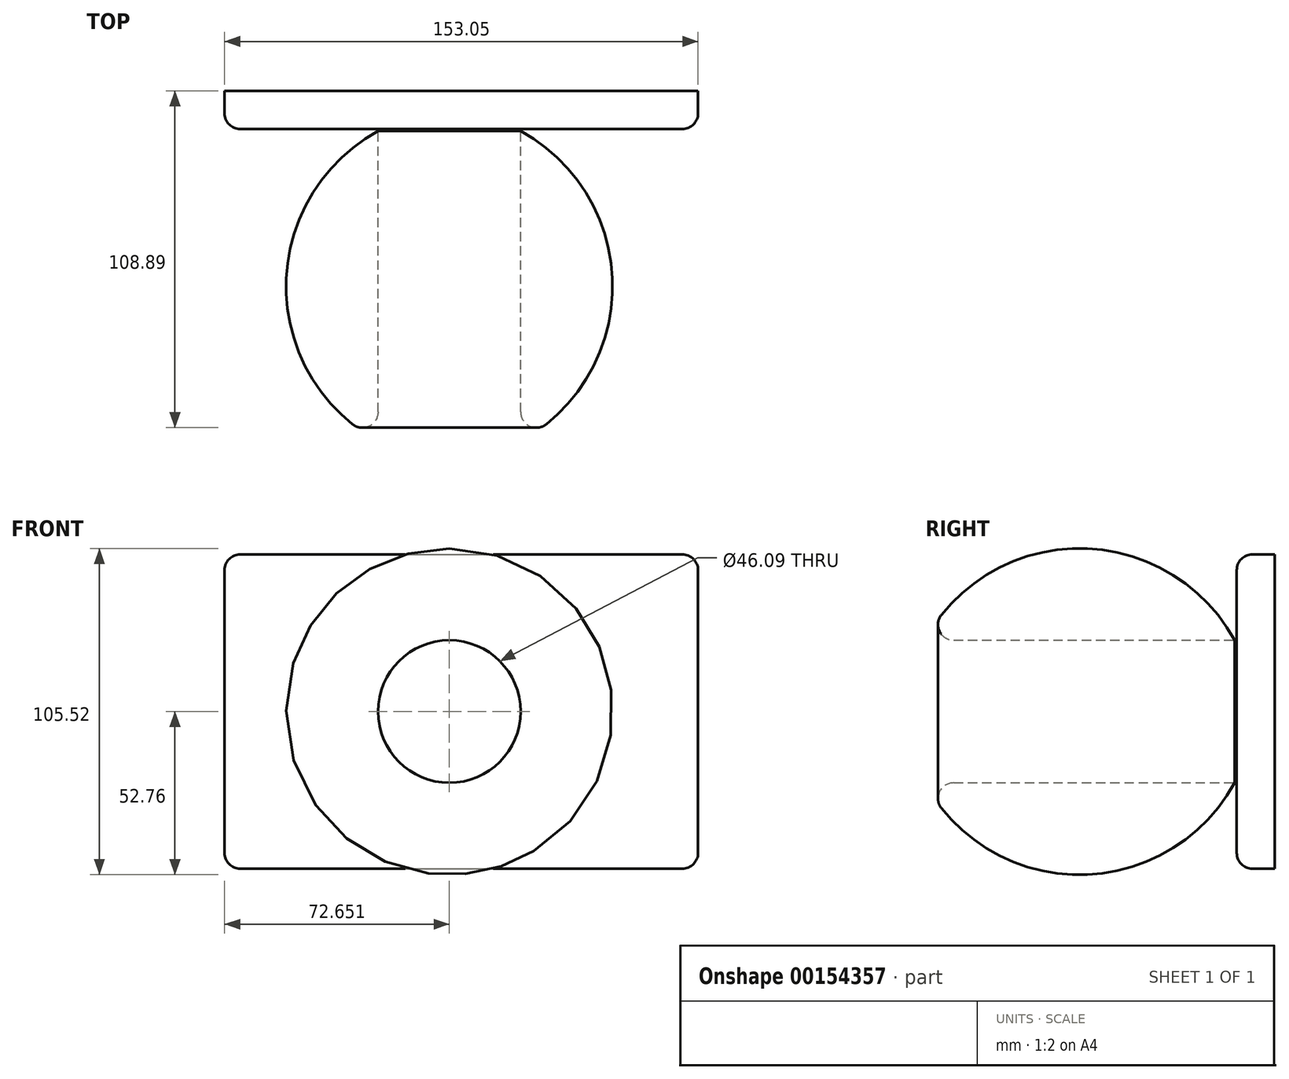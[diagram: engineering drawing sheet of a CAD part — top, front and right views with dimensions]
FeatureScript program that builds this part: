
annotation { "Feature Type Name" : "Feature", "Feature Type Description" : "" }
export const myFeature = defineFeature(function(context is Context, id is Id, definition is map)
    precondition{}
    {
        {
            var Q0;
            Q0=qCreatedBy(makeId("Top.planeOp"),FACE);
            var sketch = newSketch(context, id + "F0", { "sketchPlane" : qUnion([Q0])});
            skLineSegment(sketch, "E0", {"start": v(-59.4, 58.59) * mm, "end": v(-59.4, -41.7) * mm});
            skLineSegment(sketch, "E1", {"start": v(-36.35, 58.59) * mm, "end": v(-36.35, -41.7) * mm});
            skArc(sketch, "E2", {"start": v(-36.35, -41.7) * mm, "mid": v(-6.64, 8.44) * mm, "end": v(-36.35, 58.59) * mm});
            skSolve(sketch);
        }
        {
            var Q0;
            Q0=makeQuery(id+"F0.imprint","IMPRINT",FACE,{"disambiguationData":[TD([[makeQuery(id+"F0.imprint","IMPRINT",EDGE,{"derivedFrom":sQuery(id+"F0.wireOp",EDGE,"E1")}),1.0]])]});
            var sketch = newSketch(context, id + "F1", { "sketchPlane" : qUnion([Q0])});
            skSolve(sketch);
        }
        {
            var Q0;
            Q0=makeQuery(id+"F1.imprint","IMPRINT",FACE,{"disambiguationData":[TD([[makeQuery(id+"F1.imprint","IMPRINT",EDGE,{"derivedFrom":makeQuery(id+"F0.imprint","IMPRINT",EDGE,{"derivedFrom":sQuery(id+"F0.wireOp",EDGE,"E1")})}),1.0]])]});
            var Q1;
            Q1=sQuery(id+"F0.wireOp",EDGE,"E0");
            revolve(context, id + "F2", {"entities" : qUnion([Q0]), "axis" : qUnion([Q1]), "revolveType" : RevolveType.FULL});
        }
        {
            var Q0;
            Q0=qCreatedBy(makeId("Top.planeOp"),FACE);
            var sketch = newSketch(context, id + "F3", { "sketchPlane" : qUnion([Q0])});
            skLineSegment(sketch, "E3.bottom", {"start": v(-81.25, 59.24) * mm, "end": v(21, 59.24) * mm});
            skLineSegment(sketch, "E3.top", {"start": v(-81.25, 71.57) * mm, "end": v(21, 71.57) * mm});
            skLineSegment(sketch, "E3.left", {"start": v(-81.25, 59.24) * mm, "end": v(-81.25, 71.57) * mm});
            skLineSegment(sketch, "E3.right", {"start": v(21, 59.24) * mm, "end": v(21, 71.57) * mm});
            skSolve(sketch);
        }
        {
            var Q0;
            Q0=makeQuery(id+"F3.imprint","IMPRINT",FACE,{"disambiguationData":[TD([[makeQuery(id+"F3.imprint","IMPRINT",EDGE,{"derivedFrom":sQuery(id+"F3.wireOp",EDGE,"E3.bottom")}),1.0]])]});
            extrude(context, id + "F4", {"entities" : qUnion([Q0]), "depth" : 25.4 * mm});
        }
        {
            var Q0;
            Q0=makeQuery(id+"F4.opExtrude","CAP_FACE",FACE,{"disambiguationData":[OSD([sQuery(id+"F3.wireOp",EDGE,"E3.bottom"),sQuery(id+"F3.wireOp",EDGE,"E3.top"),sQuery(id+"F3.wireOp",EDGE,"E3.left"),sQuery(id+"F3.wireOp",EDGE,"E3.right")])],"isStart":true});
            var sketch = newSketch(context, id + "F5", { "sketchPlane" : qUnion([Q0])});
            skSolve(sketch);
        }
        {
            var Q0;
            Q0 = qSketchRegion(id + "F5", true);
            var Q1;
            Q1=makeQuery(id+"F5.imprint","IMPRINT",FACE,{"disambiguationData":[TD([[makeQuery(id+"F5.imprint","IMPRINT",EDGE,{"derivedFrom":makeQuery(id+"F4.opExtrude","CAP_EDGE",EDGE,{"disambiguationData":[OSD([sQuery(id+"F3.wireOp",EDGE,"E3.bottom")])],"isStart":true})}),-1.0]])]});
            extrude(context, id + "F6", {"entities" : qUnion([Q0, Q1]), "operationType" : NewBodyOperationType.ADD, "depth" : 25.4 * mm});
        }
        {
            var Q0;
            {var subQ0=sQuery(id+"F3.wireOp",EDGE,"E3.left");Q0=makeQuery(id+"F6.boolean.opBoolean","MERGE",FACE,{"derivedFrom":[makeQuery(id+"F4.opExtrude","SWEPT_FACE",FACE,{"disambiguationData":[OSD([subQ0])]}),makeQuery(id+"F6.opExtrude","SWEPT_FACE",FACE,{"disambiguationData":[OSD([subQ0])]})]});}
            var sketch = newSketch(context, id + "F7", { "sketchPlane" : qUnion([Q0])});
            skSolve(sketch);
        }
        {
            var Q0;
            Q0 = qSketchRegion(id + "F7", true);
            var Q1;
            {var subQ0=sQuery(id+"F3.wireOp",EDGE,"E3.left");Q1=makeQuery(id+"F7.imprint","IMPRINT",FACE,{"disambiguationData":[TD([[makeQuery(id+"F7.imprint","IMPRINT",EDGE,{"derivedFrom":makeQuery(id+"F4.opExtrude","CAP_EDGE",EDGE,{"disambiguationData":[OSD([subQ0])],"isStart":false})}),1.0]])]});}
            extrude(context, id + "F8", {"entities" : qUnion([Q0, Q1]), "operationType" : NewBodyOperationType.ADD, "depth" : 25.4 * mm});
        }
        {
            var Q0;
            Q0=makeQuery(id+"F8.opExtrude","CAP_FACE",FACE,{"disambiguationData":[OSD([sQuery(id+"F3.wireOp",EDGE,"E3.bottom"),sQuery(id+"F3.wireOp",EDGE,"E3.top"),sQuery(id+"F3.wireOp",EDGE,"E3.left")])],"isStart":false});
            extrude(context, id + "F9", {"entities" : qUnion([Q0]), "operationType" : NewBodyOperationType.ADD, "depth" : 25.4 * mm});
        }
        {
            var Q0;
            {var subQ0=sQuery(id+"F3.wireOp",EDGE,"E3.left");var subQ1=makeQuery(id+"F7.imprint","IMPRINT",EDGE,{"derivedFrom":makeQuery(id+"F6.opExtrude","CAP_EDGE",EDGE,{"disambiguationData":[OSD([subQ0])],"isStart":false})});Q0=makeQuery(id+"F9.boolean.opBoolean","MERGE",FACE,{"derivedFrom":[makeQuery(id+"F8.boolean.opBoolean","MERGE",FACE,{"derivedFrom":[makeQuery(id+"F6.opExtrude","CAP_FACE",FACE,{"disambiguationData":[OSD([sQuery(id+"F3.wireOp",EDGE,"E3.bottom"),sQuery(id+"F3.wireOp",EDGE,"E3.top"),subQ0,sQuery(id+"F3.wireOp",EDGE,"E3.right")])],"isStart":false}),makeQuery(id+"F8.opExtrude","SWEPT_FACE",FACE,{"disambiguationData":[OSD([subQ0]),TDD([subQ1])]})]}),makeQuery(id+"F9.opExtrude","SWEPT_FACE",FACE,{"disambiguationData":[OSD([subQ0]),TDD([makeQuery(id+"F8.opExtrude","CAP_EDGE",EDGE,{"disambiguationData":[OSD([subQ0]),TDD([subQ1])],"isStart":false})])]})]});}
            extrude(context, id + "F10", {"entities" : qUnion([Q0]), "operationType" : NewBodyOperationType.ADD, "depth" : 25.4 * mm});
        }
        {
            var Q0;
            {var subQ0=sQuery(id+"F3.wireOp",EDGE,"E3.left");var subQ1=makeQuery(id+"F7.imprint","IMPRINT",EDGE,{"derivedFrom":makeQuery(id+"F4.opExtrude","CAP_EDGE",EDGE,{"disambiguationData":[OSD([subQ0])],"isStart":false})});Q0=makeQuery(id+"F9.boolean.opBoolean","MERGE",FACE,{"derivedFrom":[makeQuery(id+"F8.boolean.opBoolean","MERGE",FACE,{"derivedFrom":[makeQuery(id+"F4.opExtrude","CAP_FACE",FACE,{"disambiguationData":[OSD([sQuery(id+"F3.wireOp",EDGE,"E3.bottom"),sQuery(id+"F3.wireOp",EDGE,"E3.top"),subQ0,sQuery(id+"F3.wireOp",EDGE,"E3.right")])],"isStart":false}),makeQuery(id+"F8.opExtrude","SWEPT_FACE",FACE,{"disambiguationData":[OSD([subQ0]),TDD([subQ1])]})]}),makeQuery(id+"F9.opExtrude","SWEPT_FACE",FACE,{"disambiguationData":[OSD([subQ0]),TDD([makeQuery(id+"F8.opExtrude","CAP_EDGE",EDGE,{"disambiguationData":[OSD([subQ0]),TDD([subQ1])],"isStart":false})])]})]});}
            extrude(context, id + "F11", {"entities" : qUnion([Q0]), "operationType" : NewBodyOperationType.ADD, "depth" : 25.4 * mm});
        }
        {
            var Q0;
            Q0=makeQuery(id+"F11.opExtrude","CAP_EDGE",EDGE,{"disambiguationData":[OSD([sQuery(id+"F3.wireOp",EDGE,"E3.bottom"),sQuery(id+"F3.wireOp",EDGE,"E3.left")])],"isStart":false});
            var Q1;
            {var subQ0=sQuery(id+"F3.wireOp",EDGE,"E3.left");var subQ1=sQuery(id+"F3.wireOp",EDGE,"E3.bottom");Q1=makeQuery(id+"F11.boolean.opBoolean","MERGE",EDGE,{"derivedFrom":[makeQuery(id+"F10.boolean.opBoolean","MERGE",EDGE,{"derivedFrom":[makeQuery(id+"F9.opExtrude","CAP_EDGE",EDGE,{"disambiguationData":[OSD([subQ1,subQ0])],"isStart":false}),makeQuery(id+"F10.opExtrude","SWEPT_EDGE",EDGE,{"disambiguationData":[OSD([subQ1,subQ0])]})]}),makeQuery(id+"F11.opExtrude","SWEPT_EDGE",EDGE,{"disambiguationData":[OSD([subQ1,subQ0])]})]});}
            var Q2;
            Q2=makeQuery(id+"F10.opExtrude","CAP_EDGE",EDGE,{"disambiguationData":[OSD([sQuery(id+"F3.wireOp",EDGE,"E3.bottom"),sQuery(id+"F3.wireOp",EDGE,"E3.left")])],"isStart":false});
            var Q3;
            {var subQ0=sQuery(id+"F3.wireOp",EDGE,"E3.right");var subQ1=sQuery(id+"F3.wireOp",EDGE,"E3.bottom");Q3=makeQuery(id+"F11.boolean.opBoolean","MERGE",EDGE,{"derivedFrom":[makeQuery(id+"F10.boolean.opBoolean","MERGE",EDGE,{"derivedFrom":[makeQuery(id+"F6.boolean.opBoolean","MERGE",EDGE,{"derivedFrom":[makeQuery(id+"F4.opExtrude","SWEPT_EDGE",EDGE,{"disambiguationData":[OSD([subQ1,subQ0])]}),makeQuery(id+"F6.opExtrude","SWEPT_EDGE",EDGE,{"disambiguationData":[OSD([subQ1,subQ0])]})]}),makeQuery(id+"F10.opExtrude","SWEPT_EDGE",EDGE,{"disambiguationData":[OSD([subQ1,subQ0])]})]}),makeQuery(id+"F11.opExtrude","SWEPT_EDGE",EDGE,{"disambiguationData":[OSD([subQ1,subQ0])]})]});}
            var Q4;
            Q4=makeQuery(id+"F10.opExtrude","CAP_EDGE",EDGE,{"disambiguationData":[OSD([sQuery(id+"F3.wireOp",EDGE,"E3.right")])],"isStart":false});
            var Q5;
            Q5=makeQuery(id+"F10.opExtrude","CAP_EDGE",EDGE,{"disambiguationData":[OSD([sQuery(id+"F3.wireOp",EDGE,"E3.left")])],"isStart":false});
            var Q6;
            Q6=makeQuery(id+"F11.opExtrude","CAP_EDGE",EDGE,{"disambiguationData":[OSD([sQuery(id+"F3.wireOp",EDGE,"E3.right")])],"isStart":false});
            var Q7;
            Q7=makeQuery(id+"F11.opExtrude","CAP_EDGE",EDGE,{"disambiguationData":[OSD([sQuery(id+"F3.wireOp",EDGE,"E3.left")])],"isStart":false});
            fillet(context, id + "F12", {"entities" : qUnion([Q0, Q1, Q2, Q3, Q4, Q5, Q6, Q7]), "radius" : 5.08 * mm, "tangentPropagation" : true, "allowEdgeOverflow" : false});
        }
        {
            var Q0;
            {var subQ0=sQuery(id+"F0.wireOp",EDGE,"E2");var subQ1=sQuery(id+"F0.wireOp",EDGE,"E1");Q0=makeQuery(id+"F2.opRevolve","SWEPT_EDGE",EDGE,{"disambiguationData":[OSD([subQ1,subQ0]),TDD([makeQuery(id+"F1.imprint","INTERSECT",VERTEX,{"disambiguationData":[OD(1.0)],"derivedFrom":[makeQuery(id+"F0.imprint","IMPRINT",EDGE,{"derivedFrom":subQ1}),makeQuery(id+"F0.imprint","IMPRINT",EDGE,{"derivedFrom":subQ0})]})])]});}
            fillet(context, id + "F13", {"entities" : qUnion([Q0]), "radius" : 5.08 * mm, "tangentPropagation" : true, "allowEdgeOverflow" : false});
        }
    });
